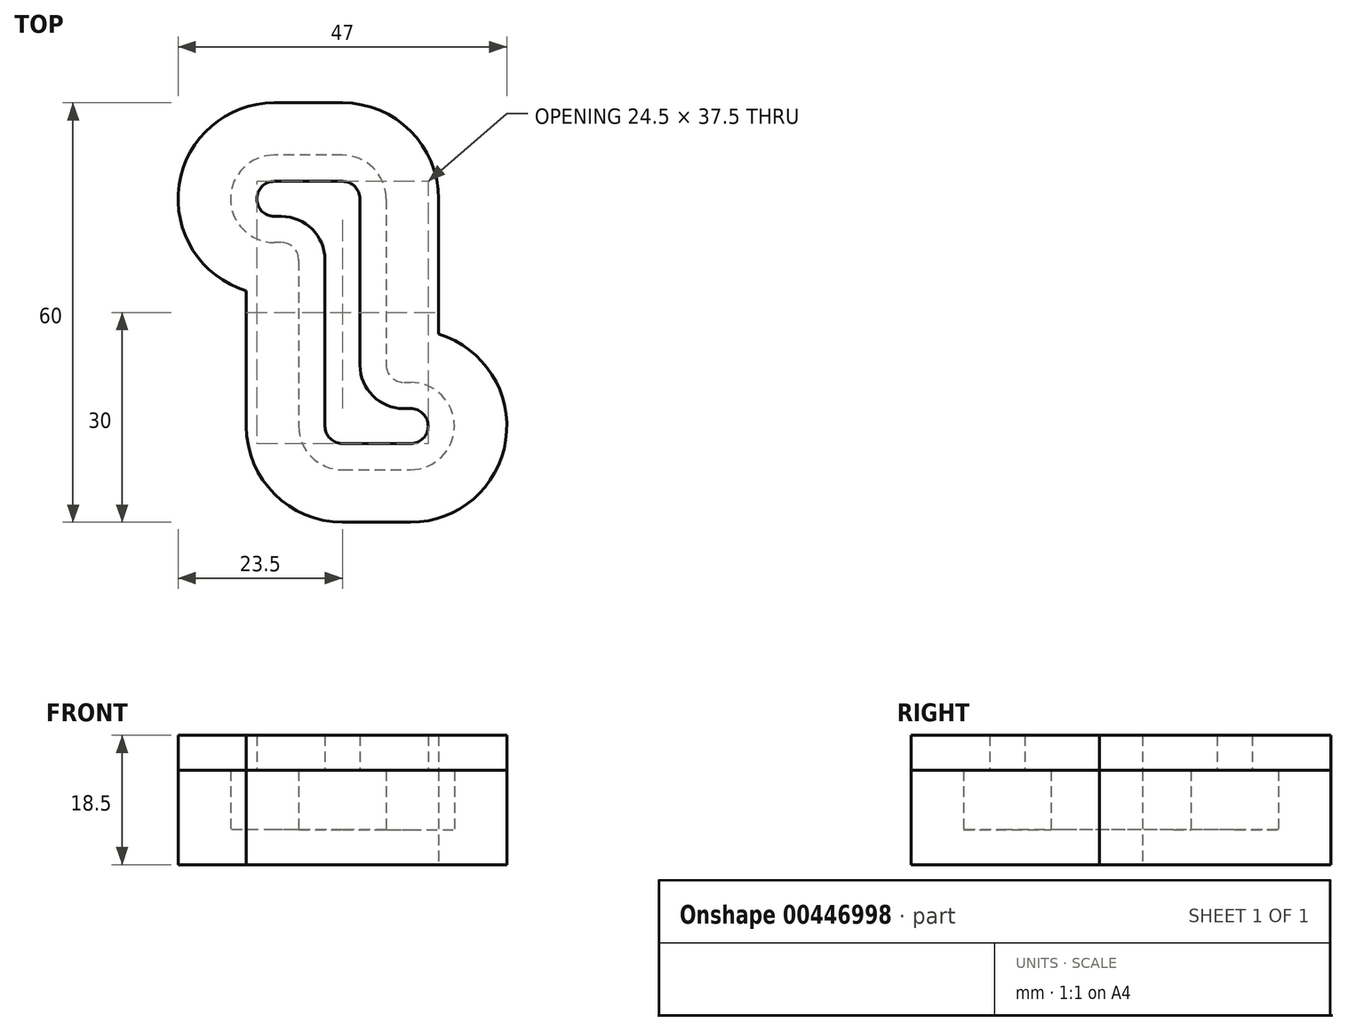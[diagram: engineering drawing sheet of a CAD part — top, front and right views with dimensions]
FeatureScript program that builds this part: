
annotation { "Feature Type Name" : "Feature", "Feature Type Description" : "" }
export const myFeature = defineFeature(function(context is Context, id is Id, definition is map)
    precondition{}
    {
        {
            var Q0;
            Q0=qCreatedBy(makeId("Top.planeOp"),FACE);
            var sketch = newSketch(context, id + "F0", { "sketchPlane" : qUnion([Q0])});
            skArc(sketch, "E0", {"start": v(-9.75, 22.5) * mm, "mid": v(-16, 16.25) * mm, "end": v(-9.75, 10) * mm});
            skArc(sketch, "E1", {"start": v(6.25, 16.25) * mm, "mid": v(4.42, 20.67) * mm, "end": v(0, 22.5) * mm});
            skArc(sketch, "E2", {"start": v(-6.25, -16.25) * mm, "mid": v(-4.42, -20.67) * mm, "end": v(0, -22.5) * mm});
            skArc(sketch, "E3", {"start": v(9.75, -22.5) * mm, "mid": v(16, -16.25) * mm, "end": v(9.75, -10) * mm});
            skLineSegment(sketch, "E4", {"start": v(-6.25, 7.5) * mm, "end": v(-6.25, -16.25) * mm});
            skLineSegment(sketch, "E5", {"start": v(6.25, 16.25) * mm, "end": v(6.25, -7.5) * mm});
            skLineSegment(sketch, "E6", {"start": v(-8.75, 10) * mm, "end": v(-9.75, 10) * mm});
            skLineSegment(sketch, "E7", {"start": v(0, 22.5) * mm, "end": v(-9.75, 22.5) * mm});
            skLineSegment(sketch, "E8", {"start": v(0, -22.5) * mm, "end": v(9.75, -22.5) * mm});
            skPoint(sketch, "E9.orphan", {"position": v(-6.25, 16.25) * mm});
            skPoint(sketch, "E10.orphan", {"position": v(0, 10) * mm});
            skPoint(sketch, "E11.orphan", {"position": v(0, -10) * mm});
            skLineSegment(sketch, "E12", {"start": v(8.75, -10) * mm, "end": v(9.75, -10) * mm});
            skPoint(sketch, "E13.visualSharp", {"position": v(6.25, -10) * mm});
            skArc(sketch, "E13.filletArc", {"start": v(6.25, -7.5) * mm, "mid": v(6.98, -9.27) * mm, "end": v(8.75, -10) * mm});
            skPoint(sketch, "E14.visualSharp", {"position": v(-6.25, 10) * mm});
            skArc(sketch, "E14.filletArc", {"start": v(-6.25, 7.5) * mm, "mid": v(-6.98, 9.27) * mm, "end": v(-8.75, 10) * mm});
            skLineSegment(sketch, "E15.0", {"start": v(0, 30) * mm, "end": v(-9.75, 30) * mm});
            skArc(sketch, "E15.1", {"start": v(13.75, 16.25) * mm, "mid": v(9.72, 25.97) * mm, "end": v(0, 30) * mm});
            skArc(sketch, "E15.2", {"start": v(-9.75, 30) * mm, "mid": v(-23.35, 18.27) * mm, "end": v(-13.75, 3.1) * mm});
            skLineSegment(sketch, "E15.3", {"start": v(13.75, 16.25) * mm, "end": v(13.75, -3.1) * mm});
            skLineSegment(sketch, "E15.4", {"start": v(-13.75, 3.1) * mm, "end": v(-13.75, -16.25) * mm});
            skArc(sketch, "E15.5", {"start": v(-13.75, -16.25) * mm, "mid": v(-9.72, -25.97) * mm, "end": v(0, -30) * mm});
            skLineSegment(sketch, "E15.6", {"start": v(0, -30) * mm, "end": v(9.75, -30) * mm});
            skArc(sketch, "E15.7", {"start": v(9.75, -30) * mm, "mid": v(23.35, -18.27) * mm, "end": v(13.75, -3.1) * mm});
            skArc(sketch, "E16.0", {"start": v(-2.5, 7.5) * mm, "mid": v(-4.33, 11.92) * mm, "end": v(-8.75, 13.75) * mm});
            skLineSegment(sketch, "E16.1", {"start": v(8.75, -13.75) * mm, "end": v(9.75, -13.75) * mm});
            skArc(sketch, "E16.2", {"start": v(9.75, -18.75) * mm, "mid": v(12.25, -16.25) * mm, "end": v(9.75, -13.75) * mm});
            skLineSegment(sketch, "E16.3", {"start": v(0, -18.75) * mm, "end": v(9.75, -18.75) * mm});
            skArc(sketch, "E16.4", {"start": v(-2.5, -16.25) * mm, "mid": v(-1.77, -18.02) * mm, "end": v(0, -18.75) * mm});
            skArc(sketch, "E16.5", {"start": v(2.5, -7.5) * mm, "mid": v(4.33, -11.92) * mm, "end": v(8.75, -13.75) * mm});
            skLineSegment(sketch, "E16.6", {"start": v(-2.5, 7.5) * mm, "end": v(-2.5, -16.25) * mm});
            skLineSegment(sketch, "E16.7", {"start": v(2.5, 16.25) * mm, "end": v(2.5, -7.5) * mm});
            skArc(sketch, "E16.8", {"start": v(2.5, 16.25) * mm, "mid": v(1.77, 18.02) * mm, "end": v(0, 18.75) * mm});
            skLineSegment(sketch, "E16.9", {"start": v(0, 18.75) * mm, "end": v(-9.75, 18.75) * mm});
            skArc(sketch, "E16.10", {"start": v(-9.75, 18.75) * mm, "mid": v(-12.25, 16.25) * mm, "end": v(-9.75, 13.75) * mm});
            skLineSegment(sketch, "E16.11", {"start": v(-8.75, 13.75) * mm, "end": v(-9.75, 13.75) * mm});
            skSolve(sketch);
        }
        {
            var Q0;
            Q0 = qSketchRegion(id + "F0", true);
            var Q1;
            Q1=makeQuery(id+"F0.imprint","IMPRINT",FACE,{"disambiguationData":[TD([[makeQuery(id+"F0.imprint","IMPRINT",EDGE,{"derivedFrom":sQuery(id+"F0.wireOp",EDGE,"E16.0")}),-1.0]])]});
            var Q2;
            Q2=makeQuery(id+"F0.imprint","IMPRINT",FACE,{"disambiguationData":[TD([[makeQuery(id+"F0.imprint","IMPRINT",EDGE,{"derivedFrom":sQuery(id+"F0.wireOp",EDGE,"E0")}),1.0]])]});
            extrude(context, id + "F1", {"entities" : qUnion([Q0, Q1, Q2]), "depth" : 5 * mm});
        }
        {
            var Q0;
            Q0 = qSketchRegion(id + "F0", true);
            extrude(context, id + "F2", {"entities" : qUnion([Q0]), "operationType" : NewBodyOperationType.ADD, "depth" : 13.5 * mm, "hasSecondDirection" : true, "secondDirectionOppositeDirection" : false, "secondDirectionDepth" : 5 * mm});
        }
        {
            var Q0;
            Q0=makeQuery(id+"F0.imprint","IMPRINT",FACE,{"disambiguationData":[TD([[makeQuery(id+"F0.imprint","IMPRINT",EDGE,{"derivedFrom":sQuery(id+"F0.wireOp",EDGE,"E0")}),1.0]])]});
            var Q1;
            Q1=makeQuery(id+"F0.imprint","IMPRINT",FACE,{"disambiguationData":[TD([[makeQuery(id+"F0.imprint","IMPRINT",EDGE,{"derivedFrom":sQuery(id+"F0.wireOp",EDGE,"E0")}),-1.0]])]});
            extrude(context, id + "F3", {"entities" : qUnion([Q0, Q1]), "depth" : 18.5 * mm, "hasSecondDirection" : true, "secondDirectionOppositeDirection" : false, "secondDirectionDepth" : 13.5 * mm});
        }
    });
